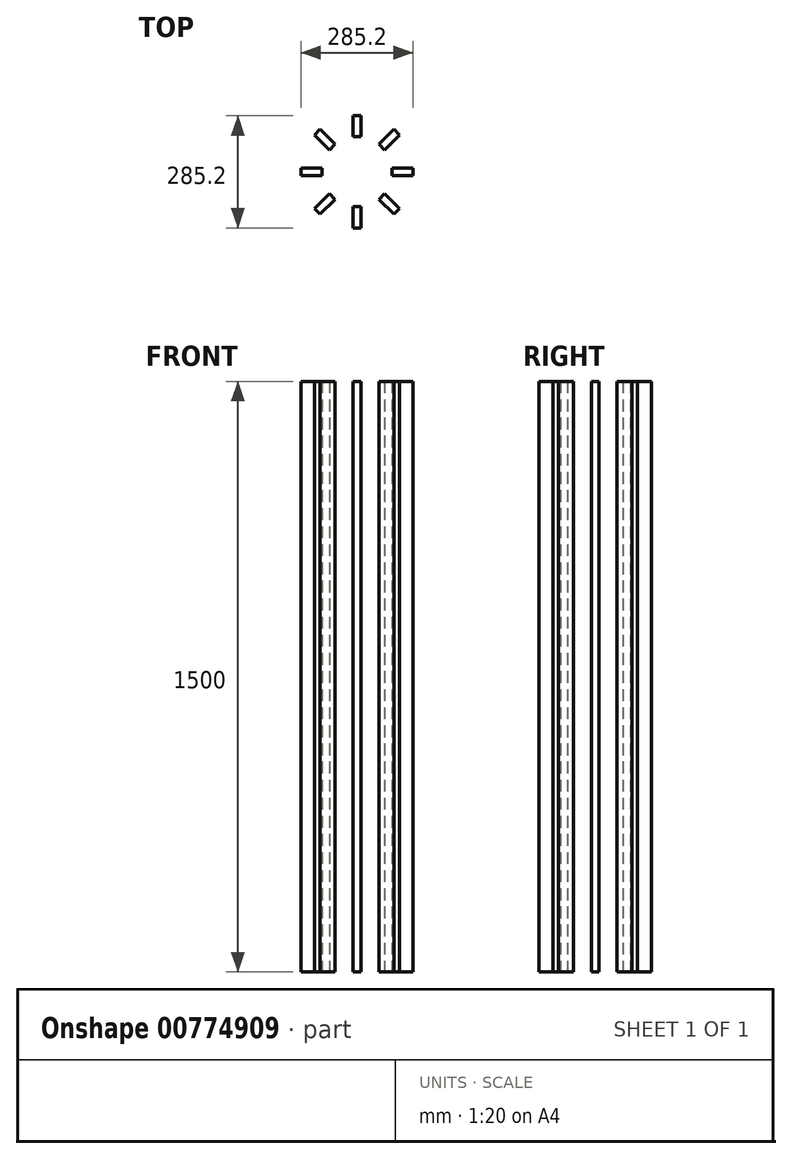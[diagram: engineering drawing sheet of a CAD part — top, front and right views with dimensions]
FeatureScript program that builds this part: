
annotation { "Feature Type Name" : "Feature", "Feature Type Description" : "" }
export const myFeature = defineFeature(function(context is Context, id is Id, definition is map)
    precondition{}
    {
        {
            var Q0;
            Q0=qCreatedBy(makeId("Top.planeOp"),FACE);
            var sketch = newSketch(context, id + "F0", { "sketchPlane" : qUnion([Q0])});
            skCircle(sketch, "E0", {"center": v(0, 0) * mm, "radius": 142.95 * mm});
            skCircle(sketch, "E1", {"center": v(0, 0) * mm, "radius": 88.9 * mm});
            skLineSegment(sketch, "E2", {"start": v(0, 0) * mm, "end": v(0, 142.95) * mm, "construction": true});
            skLineSegment(sketch, "E3", {"start": v(0, 0) * mm, "end": v(-88.9, 0) * mm, "construction": true});
            skLineSegment(sketch, "E4", {"start": v(0, 0) * mm, "end": v(88.9, 0) * mm, "construction": true});
            skLineSegment(sketch, "E5", {"start": v(0, 0) * mm, "end": v(0, -88.9) * mm, "construction": true});
            skLineSegment(sketch, "E6.bottom", {"start": v(0, -88.9) * mm, "end": v(10, -88.9) * mm});
            skLineSegment(sketch, "E6.top", {"start": v(0, -142.6) * mm, "end": v(10, -142.6) * mm});
            skLineSegment(sketch, "E6.right", {"start": v(10, -88.9) * mm, "end": v(10, -142.6) * mm});
            skPoint(sketch, "E7", {"position": v(0, -88.9) * mm});
            skLineSegment(sketch, "E8.MirrorCS", {"start": v(-10, -88.9) * mm, "end": v(-10, -142.6) * mm});
            skLineSegment(sketch, "E9", {"start": v(-10, -88.9) * mm, "end": v(0, -88.9) * mm});
            skLineSegment(sketch, "E10", {"start": v(0, -142.6) * mm, "end": v(-10, -142.6) * mm});
            skLineSegment(sketch, "E11.trimOffspring", {"start": v(0, -142.6) * mm, "end": v(0, -142.95) * mm, "construction": true});
            skLineSegment(sketch, "E12.1.0", {"start": v(55.8, -69.93) * mm, "end": v(93.76, -107.9) * mm});
            skLineSegment(sketch, "E12.1.1", {"start": v(55.8, -69.93) * mm, "end": v(62.86, -62.86) * mm});
            skLineSegment(sketch, "E12.1.2", {"start": v(69.93, -55.8) * mm, "end": v(107.9, -93.76) * mm});
            skLineSegment(sketch, "E12.1.3", {"start": v(62.86, -62.86) * mm, "end": v(69.93, -55.8) * mm});
            skLineSegment(sketch, "E12.1.4", {"start": v(100.83, -100.83) * mm, "end": v(107.9, -93.76) * mm});
            skLineSegment(sketch, "E12.1.5", {"start": v(100.83, -100.83) * mm, "end": v(93.76, -107.9) * mm});
            skLineSegment(sketch, "E12.2.0", {"start": v(88.9, -10) * mm, "end": v(142.6, -10) * mm});
            skLineSegment(sketch, "E12.2.1", {"start": v(88.9, -10) * mm, "end": v(88.9, 0) * mm});
            skLineSegment(sketch, "E12.2.2", {"start": v(88.9, 10) * mm, "end": v(142.6, 10) * mm});
            skLineSegment(sketch, "E12.2.3", {"start": v(88.9, 0) * mm, "end": v(88.9, 10) * mm});
            skLineSegment(sketch, "E12.2.4", {"start": v(142.6, 0) * mm, "end": v(142.6, 10) * mm});
            skLineSegment(sketch, "E12.2.5", {"start": v(142.6, 0) * mm, "end": v(142.6, -10) * mm});
            skLineSegment(sketch, "E12.3.0", {"start": v(69.93, 55.8) * mm, "end": v(107.9, 93.76) * mm});
            skLineSegment(sketch, "E12.3.1", {"start": v(69.93, 55.8) * mm, "end": v(62.86, 62.86) * mm});
            skLineSegment(sketch, "E12.3.2", {"start": v(55.8, 69.93) * mm, "end": v(93.76, 107.9) * mm});
            skLineSegment(sketch, "E12.3.3", {"start": v(62.86, 62.86) * mm, "end": v(55.8, 69.93) * mm});
            skLineSegment(sketch, "E12.3.4", {"start": v(100.83, 100.83) * mm, "end": v(93.76, 107.9) * mm});
            skLineSegment(sketch, "E12.3.5", {"start": v(100.83, 100.83) * mm, "end": v(107.9, 93.76) * mm});
            skLineSegment(sketch, "E12.4.0", {"start": v(10, 88.9) * mm, "end": v(10, 142.6) * mm});
            skLineSegment(sketch, "E12.4.1", {"start": v(10, 88.9) * mm, "end": v(0, 88.9) * mm});
            skLineSegment(sketch, "E12.4.2", {"start": v(-10, 88.9) * mm, "end": v(-10, 142.6) * mm});
            skLineSegment(sketch, "E12.4.3", {"start": v(0, 88.9) * mm, "end": v(-10, 88.9) * mm});
            skLineSegment(sketch, "E12.4.4", {"start": v(0, 142.6) * mm, "end": v(-10, 142.6) * mm});
            skLineSegment(sketch, "E12.4.5", {"start": v(0, 142.6) * mm, "end": v(10, 142.6) * mm});
            skLineSegment(sketch, "E12.5.0", {"start": v(-55.8, 69.93) * mm, "end": v(-93.76, 107.9) * mm});
            skLineSegment(sketch, "E12.5.1", {"start": v(-55.8, 69.93) * mm, "end": v(-62.86, 62.86) * mm});
            skLineSegment(sketch, "E12.5.2", {"start": v(-69.93, 55.8) * mm, "end": v(-107.9, 93.76) * mm});
            skLineSegment(sketch, "E12.5.3", {"start": v(-62.86, 62.86) * mm, "end": v(-69.93, 55.8) * mm});
            skLineSegment(sketch, "E12.5.4", {"start": v(-100.83, 100.83) * mm, "end": v(-107.9, 93.76) * mm});
            skLineSegment(sketch, "E12.5.5", {"start": v(-100.83, 100.83) * mm, "end": v(-93.76, 107.9) * mm});
            skLineSegment(sketch, "E13.2.6.0", {"start": v(-88.9, 10) * mm, "end": v(-142.6, 10) * mm});
            skLineSegment(sketch, "E13.3.6.0", {"start": v(-88.9, 10) * mm, "end": v(-88.9, 0) * mm});
            skLineSegment(sketch, "E13.6.6.0", {"start": v(-88.9, -10) * mm, "end": v(-142.6, -10) * mm});
            skLineSegment(sketch, "E13.9.6.0", {"start": v(-88.9, 0) * mm, "end": v(-88.9, -10) * mm});
            skLineSegment(sketch, "E13.12.6.0", {"start": v(-142.6, 0) * mm, "end": v(-142.6, -10) * mm});
            skLineSegment(sketch, "E13.15.6.0", {"start": v(-142.6, 0) * mm, "end": v(-142.6, 10) * mm});
            skLineSegment(sketch, "E13.2.7.0", {"start": v(-69.93, -55.8) * mm, "end": v(-107.9, -93.76) * mm});
            skLineSegment(sketch, "E13.3.7.0", {"start": v(-69.93, -55.8) * mm, "end": v(-62.86, -62.86) * mm});
            skLineSegment(sketch, "E13.6.7.0", {"start": v(-55.8, -69.93) * mm, "end": v(-93.76, -107.9) * mm});
            skLineSegment(sketch, "E13.9.7.0", {"start": v(-62.86, -62.86) * mm, "end": v(-55.8, -69.93) * mm});
            skLineSegment(sketch, "E13.12.7.0", {"start": v(-100.83, -100.83) * mm, "end": v(-93.76, -107.9) * mm});
            skLineSegment(sketch, "E13.15.7.0", {"start": v(-100.83, -100.83) * mm, "end": v(-107.9, -93.76) * mm});
            skSolve(sketch);
        }
        {
            var Q0;
            Q0=makeQuery(id+"F0.imprint","IMPRINT",FACE,{"disambiguationData":[TD([[makeQuery(id+"F0.imprint","IMPRINT",EDGE,{"derivedFrom":sQuery(id+"F0.wireOp",EDGE,"E12.4.0")}),1.0]])]});
            var Q1;
            Q1=makeQuery(id+"F0.imprint","IMPRINT",FACE,{"disambiguationData":[TD([[makeQuery(id+"F0.imprint","IMPRINT",EDGE,{"derivedFrom":sQuery(id+"F0.wireOp",EDGE,"E12.3.0")}),1.0]])]});
            var Q2;
            Q2=makeQuery(id+"F0.imprint","IMPRINT",FACE,{"disambiguationData":[TD([[makeQuery(id+"F0.imprint","IMPRINT",EDGE,{"derivedFrom":sQuery(id+"F0.wireOp",EDGE,"E12.2.0")}),1.0]])]});
            var Q3;
            Q3=makeQuery(id+"F0.imprint","IMPRINT",FACE,{"disambiguationData":[TD([[makeQuery(id+"F0.imprint","IMPRINT",EDGE,{"derivedFrom":sQuery(id+"F0.wireOp",EDGE,"E12.1.0")}),1.0]])]});
            var Q4;
            Q4=makeQuery(id+"F0.imprint","IMPRINT",FACE,{"disambiguationData":[TD([[makeQuery(id+"F0.imprint","IMPRINT",EDGE,{"derivedFrom":sQuery(id+"F0.wireOp",EDGE,"E6.bottom")}),-1.0]])]});
            var Q5;
            Q5=makeQuery(id+"F0.imprint","IMPRINT",FACE,{"disambiguationData":[TD([[makeQuery(id+"F0.imprint","IMPRINT",EDGE,{"derivedFrom":sQuery(id+"F0.wireOp",EDGE,"E12.5.0")}),1.0]])]});
            var Q6;
            Q6=makeQuery(id+"F0.imprint","IMPRINT",FACE,{"disambiguationData":[TD([[makeQuery(id+"F0.imprint","IMPRINT",EDGE,{"derivedFrom":sQuery(id+"F0.wireOp",EDGE,"E13.2.6.0")}),1.0]])]});
            var Q7;
            Q7=makeQuery(id+"F0.imprint","IMPRINT",FACE,{"disambiguationData":[TD([[makeQuery(id+"F0.imprint","IMPRINT",EDGE,{"derivedFrom":sQuery(id+"F0.wireOp",EDGE,"E13.2.7.0")}),1.0]])]});
            extrude(context, id + "F1", {"entities" : qUnion([Q0, Q1, Q2, Q3, Q4, Q5, Q6, Q7]), "depth" : 1500 * mm, "offsetDistance" : 25 * mm});
        }
    });
